# Revit family: Unterflurdose UGD350-3 für GES9_55
name_source: partatom
category: Generic Models
revit_build: Autodesk Revit 2015 (Build: 20140606_1530(x64)
units: mm (PartAtom-declared; Revit-internal decimal feet)

## types (1)
- UGD 350-3 9R
    "A" Dimension = 467 mm  [stored 1.53215 ft]
    "B" Dimension = 467 mm  [stored 1.53215 ft]
    Article Type = UGD55 350-3 9R
    Cover Width = 373 mm  [stored 1.22375 ft]
    Cover size "a" = 244 mm  [stored 0.800525 ft]
    Cover size "b" = 244 mm  [stored 0.800525 ft]
    GTIN = 4012195678762
    Height = 70 mm  [stored 0.229659 ft]
    HeightCalc = 70 mm  [stored 0.229659 ft]
    Manufacturer = OBO Bettermann
    Manufacturer Art. No. = 7410062
    Material = Steel, Galvanized
    Size "a" = 362 mm  [stored 1.18766 ft]
    Size "b" = 383 mm  [stored 1.25656 ft]
    URL = http://www.obo-bettermann.com

note: [stored X ft] marks values corroborated as IEEE doubles in the binary element streams (Revit-internal decimal feet)

## geometry (parser evidence)
native form markers: Sweep x2
no freeform markers — native parametric forms only
